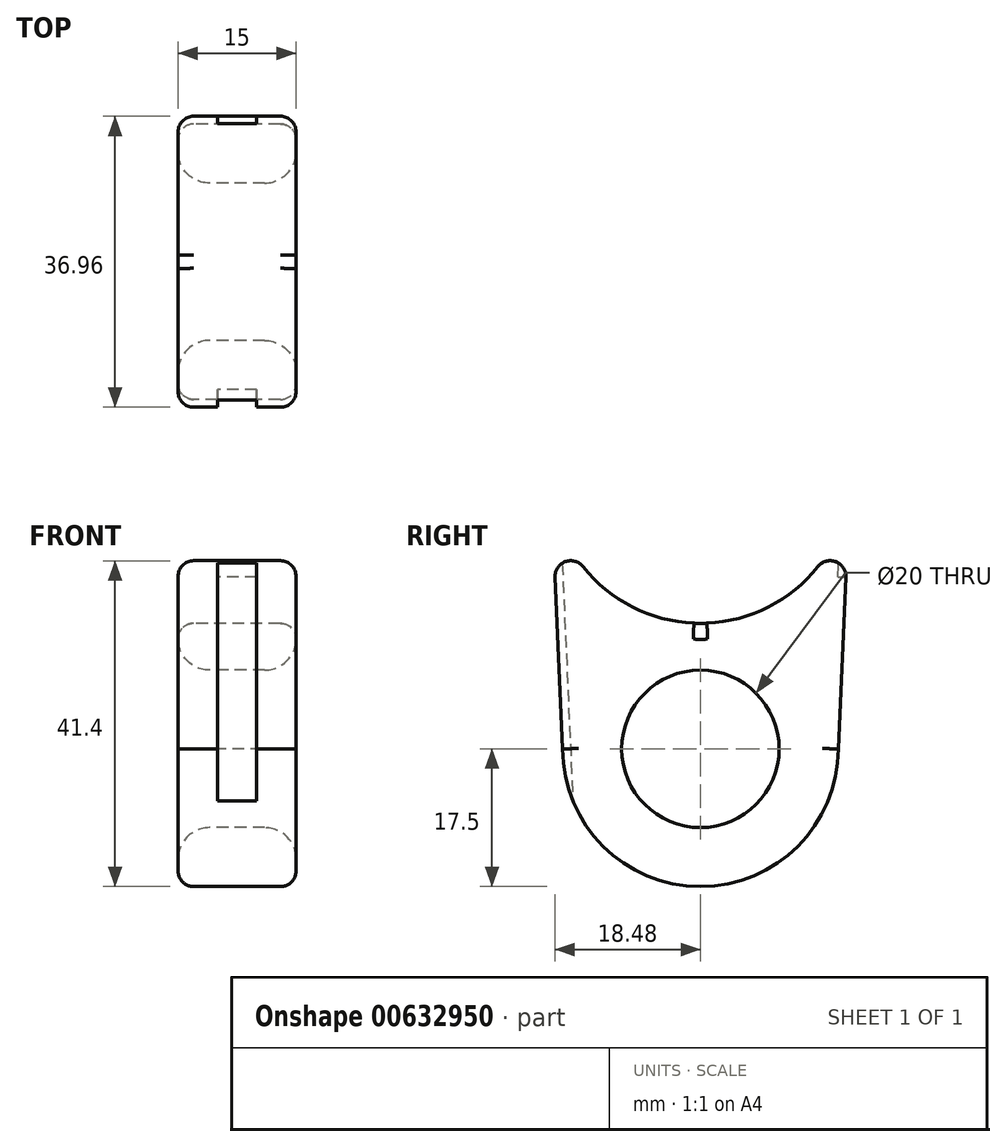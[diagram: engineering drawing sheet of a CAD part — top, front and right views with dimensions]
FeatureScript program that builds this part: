
annotation { "Feature Type Name" : "Feature", "Feature Type Description" : "" }
export const myFeature = defineFeature(function(context is Context, id is Id, definition is map)
    precondition{}
    {
        {
            var Q0;
            Q0=qCreatedBy(makeId("Right.planeOp"),FACE);
            var sketch = newSketch(context, id + "F0", { "sketchPlane" : qUnion([Q0])});
            skArc(sketch, "E0", {"start": v(-14.91, -11.85) * mm, "mid": v(0, -19.05) * mm, "end": v(14.91, -11.85) * mm});
            skCircle(sketch, "E1", {"center": v(0, -35) * mm, "radius": 10 * mm});
            skArc(sketch, "E2", {"start": v(-17.5, -35) * mm, "mid": v(0, -52.5) * mm, "end": v(17.5, -35) * mm});
            skLineSegment(sketch, "E3", {"start": v(-17.5, -35) * mm, "end": v(-18.48, -13.19) * mm});
            skLineSegment(sketch, "E4", {"start": v(17.5, -35) * mm, "end": v(18.48, -13.19) * mm});
            skPoint(sketch, "E5.visualSharp", {"position": v(-19.03, -0.85) * mm});
            skArc(sketch, "E5.filletArc", {"start": v(-14.91, -11.85) * mm, "mid": v(-17.18, -11.22) * mm, "end": v(-18.48, -13.19) * mm});
            skPoint(sketch, "E6.visualSharp", {"position": v(19.03, -0.85) * mm});
            skArc(sketch, "E6.filletArc", {"start": v(18.48, -13.19) * mm, "mid": v(17.18, -11.22) * mm, "end": v(14.91, -11.85) * mm});
            skSolve(sketch);
        }
        {
            var Q0;
            Q0=makeQuery(id+"F0.imprint","IMPRINT",FACE,{"disambiguationData":[TD([[makeQuery(id+"F0.imprint","IMPRINT",EDGE,{"derivedFrom":sQuery(id+"F0.wireOp",EDGE,"E0")}),-1.0]])]});
            extrude(context, id + "F1", {"entities" : qUnion([Q0]), "endBound" : BoundingType.SYMMETRIC, "depth" : 15 * mm, "offsetDistance" : 25 * mm});
        }
        {
            var Q0;
            Q0=makeQuery(id+"F1.opExtrude","SWEPT_FACE",FACE,{"disambiguationData":[OSD([sQuery(id+"F0.wireOp",EDGE,"E3")])]});
            var sketch = newSketch(context, id + "F2", { "sketchPlane" : qUnion([Q0])});
            skLineSegment(sketch, "E7", {"start": v(-2.5, -10.35) * mm, "end": v(-2.5, -42.35) * mm});
            skLineSegment(sketch, "E8", {"start": v(2.5, -42.35) * mm, "end": v(2.5, -10.35) * mm});
            skLineSegment(sketch, "E9", {"start": v(-2.5, -42.35) * mm, "end": v(2.5, -42.35) * mm});
            skLineSegment(sketch, "E10", {"start": v(-7.5, -10.35) * mm, "end": v(7.5, -10.35) * mm});
            skLineSegment(sketch, "E11", {"start": v(-2.5, -10.35) * mm, "end": v(2.5, -10.35) * mm});
            skSolve(sketch);
        }
        {
            var Q0;
            Q0 = qSketchRegion(id + "F2", true);
            extrude(context, id + "F3", {"entities" : qUnion([Q0]), "operationType" : NewBodyOperationType.REMOVE, "endBound" : BoundingType.SYMMETRIC, "oppositeDirection" : true, "depth" : 2 * mm, "offsetDistance" : 25 * mm});
        }
        {
            var Q0;
            Q0=makeQuery(id+"F1.opExtrude","SWEPT_FACE",FACE,{"disambiguationData":[OSD([sQuery(id+"F0.wireOp",EDGE,"E4")])]});
            var sketch = newSketch(context, id + "F4", { "sketchPlane" : qUnion([Q0])});
            skLineSegment(sketch, "E12.0", {"start": v(2.5, -12) * mm, "end": v(2.5, -43.88) * mm});
            skLineSegment(sketch, "E12.1", {"start": v(-2.5, -43.88) * mm, "end": v(-2.5, -12) * mm});
            skLineSegment(sketch, "E12.3", {"start": v(2.5, -43.88) * mm, "end": v(-2.5, -43.88) * mm});
            skLineSegment(sketch, "E13.top", {"start": v(-2.5, -43.88) * mm, "end": v(2.5, -43.88) * mm});
            skLineSegment(sketch, "E13.left", {"start": v(-2.5, -10.35) * mm, "end": v(-2.5, -43.88) * mm});
            skLineSegment(sketch, "E13.right", {"start": v(2.5, -10.35) * mm, "end": v(2.5, -43.88) * mm});
            skLineSegment(sketch, "E14.0.0", {"start": v(7.5, -12.35) * mm, "end": v(7.5, -10.35) * mm});
            skLineSegment(sketch, "E14.0.2", {"start": v(-7.5, -10.35) * mm, "end": v(-7.5, -12.35) * mm});
            skLineSegment(sketch, "E14.0.3", {"start": v(-7.5, -12.35) * mm, "end": v(7.5, -12.35) * mm});
            skLineSegment(sketch, "E15", {"start": v(-7.5, -10.35) * mm, "end": v(7.5, -10.35) * mm});
            skLineSegment(sketch, "E16", {"start": v(-2.5, -10.35) * mm, "end": v(2.5, -10.35) * mm});
            skSolve(sketch);
        }
        {
            var Q0;
            {var subQ0=sQuery(id+"F4.wireOp",EDGE,"E13.top");Q0=makeQuery(id+"F4.imprint","IMPRINT",FACE,{"disambiguationData":[TD([[makeQuery(id+"F4.imprint","IMPRINT",EDGE,{"derivedFrom":subQ0}),1.0]])]});}
            var Q1;
            {var subQ0=sQuery(id+"F4.wireOp",EDGE,"E13.left");var subQ1=sQuery(id+"F0.wireOp",EDGE,"E4");var subQ2=makeQuery(id+"F1.opExtrude","SWEPT_EDGE",EDGE,{"disambiguationData":[OSD([subQ1,sQuery(id+"F0.wireOp",EDGE,"E6.filletArc")])]});var subQ3=makeQuery(id+"F4.imprint","INTERSECT",VERTEX,{"derivedFrom":[subQ2,subQ0]});Q1=makeQuery(id+"F4.imprint","IMPRINT",FACE,{"disambiguationData":[TD([[makeQuery(id+"F4.imprint","IMPRINT",EDGE,{"disambiguationData":[TD([[subQ3,-1.0]])],"derivedFrom":subQ0}),1.0]])]});}
            var Q2;
            {var subQ0=sQuery(id+"F4.wireOp",EDGE,"E13.bottom");Q2=makeQuery(id+"F4.imprint","IMPRINT",FACE,{"disambiguationData":[TD([[makeQuery(id+"F4.imprint","IMPRINT",EDGE,{"derivedFrom":subQ0}),-1.0]])]});}
            var Q3;
            {var subQ0=sQuery(id+"F4.wireOp",EDGE,"E16");Q3=makeQuery(id+"F4.imprint","IMPRINT",FACE,{"disambiguationData":[TD([[makeQuery(id+"F4.imprint","IMPRINT",EDGE,{"derivedFrom":subQ0}),-1.0]])]});}
            extrude(context, id + "F5", {"entities" : qUnion([Q0, Q1, Q2, Q3]), "operationType" : NewBodyOperationType.REMOVE, "endBound" : BoundingType.SYMMETRIC, "oppositeDirection" : true, "depth" : 2 * mm, "offsetDistance" : 25 * mm});
        }
        {
            var Q0;
            Q0=makeQuery(id+"F1.opExtrude","CAP_EDGE",EDGE,{"disambiguationData":[OSD([sQuery(id+"F0.wireOp",EDGE,"E1")])],"isStart":false});
            var Q1;
            Q1=makeQuery(id+"F1.opExtrude","CAP_EDGE",EDGE,{"disambiguationData":[OSD([sQuery(id+"F0.wireOp",EDGE,"E1")])],"isStart":true});
            fillet(context, id + "F6", {"entities" : qUnion([Q0, Q1]), "radius" : 4 * mm, "tangentPropagation" : true, "allowEdgeOverflow" : false});
        }
        {
            var Q0;
            Q0=makeQuery(id+"F1.opExtrude","CAP_FACE",FACE,{"disambiguationData":[OSD([sQuery(id+"F0.wireOp",EDGE,"E0"),sQuery(id+"F0.wireOp",EDGE,"E1"),sQuery(id+"F0.wireOp",EDGE,"E2"),sQuery(id+"F0.wireOp",EDGE,"E3"),sQuery(id+"F0.wireOp",EDGE,"E4"),sQuery(id+"F0.wireOp",EDGE,"E5.filletArc"),sQuery(id+"F0.wireOp",EDGE,"E6.filletArc")])],"isStart":true});
            var Q1;
            Q1=makeQuery(id+"F1.opExtrude","CAP_EDGE",EDGE,{"disambiguationData":[OSD([sQuery(id+"F0.wireOp",EDGE,"E4")])],"isStart":false});
            var Q2;
            Q2=makeQuery(id+"F1.opExtrude","CAP_FACE",FACE,{"disambiguationData":[OSD([sQuery(id+"F0.wireOp",EDGE,"E0"),sQuery(id+"F0.wireOp",EDGE,"E1"),sQuery(id+"F0.wireOp",EDGE,"E2"),sQuery(id+"F0.wireOp",EDGE,"E3"),sQuery(id+"F0.wireOp",EDGE,"E4"),sQuery(id+"F0.wireOp",EDGE,"E5.filletArc"),sQuery(id+"F0.wireOp",EDGE,"E6.filletArc")])],"isStart":false});
            fillet(context, id + "F7", {"entities" : qUnion([Q0, Q1, Q2]), "radius" : 2 * mm, "tangentPropagation" : true, "allowEdgeOverflow" : false});
        }
    });
